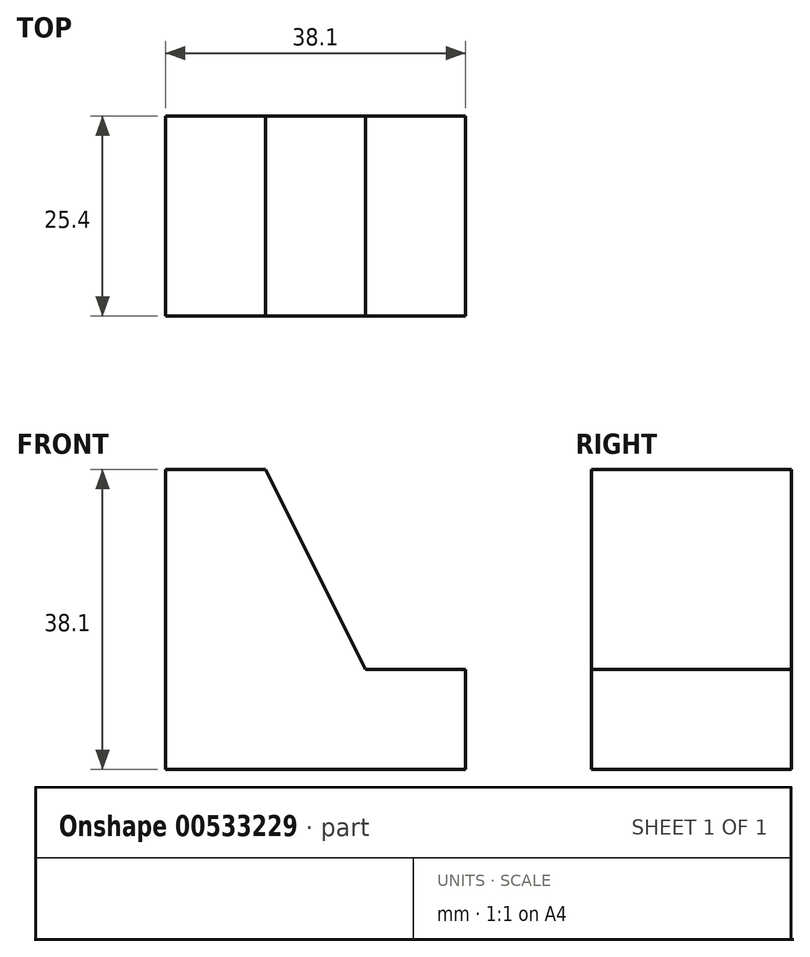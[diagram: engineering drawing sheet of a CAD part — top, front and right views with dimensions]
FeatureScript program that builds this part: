
annotation { "Feature Type Name" : "Feature", "Feature Type Description" : "" }
export const myFeature = defineFeature(function(context is Context, id is Id, definition is map)
    precondition{}
    {
        {
            var Q0;
            Q0=qCreatedBy(makeId("Front.planeOp"),FACE);
            var sketch = newSketch(context, id + "F0", { "sketchPlane" : qUnion([Q0])});
            skLineSegment(sketch, "E0", {"start": v(-62, 49.4) * mm, "end": v(-62, 11.3) * mm});
            skLineSegment(sketch, "E1", {"start": v(-62, 49.4) * mm, "end": v(-49.3, 49.4) * mm});
            skLineSegment(sketch, "E2", {"start": v(-62, 11.3) * mm, "end": v(-23.9, 11.3) * mm});
            skLineSegment(sketch, "E3", {"start": v(-23.9, 11.3) * mm, "end": v(-23.9, 24) * mm});
            skLineSegment(sketch, "E4", {"start": v(-23.9, 24) * mm, "end": v(-36.6, 24) * mm});
            skLineSegment(sketch, "E5", {"start": v(-49.3, 49.4) * mm, "end": v(-36.6, 24) * mm});
            skSolve(sketch);
        }
        {
            var Q0;
            Q0 = qSketchRegion(id + "F0", true);
            extrude(context, id + "F1", {"entities" : qUnion([Q0]), "depth" : 25.4 * mm, "offsetDistance" : 25.4 * mm});
        }
    });
